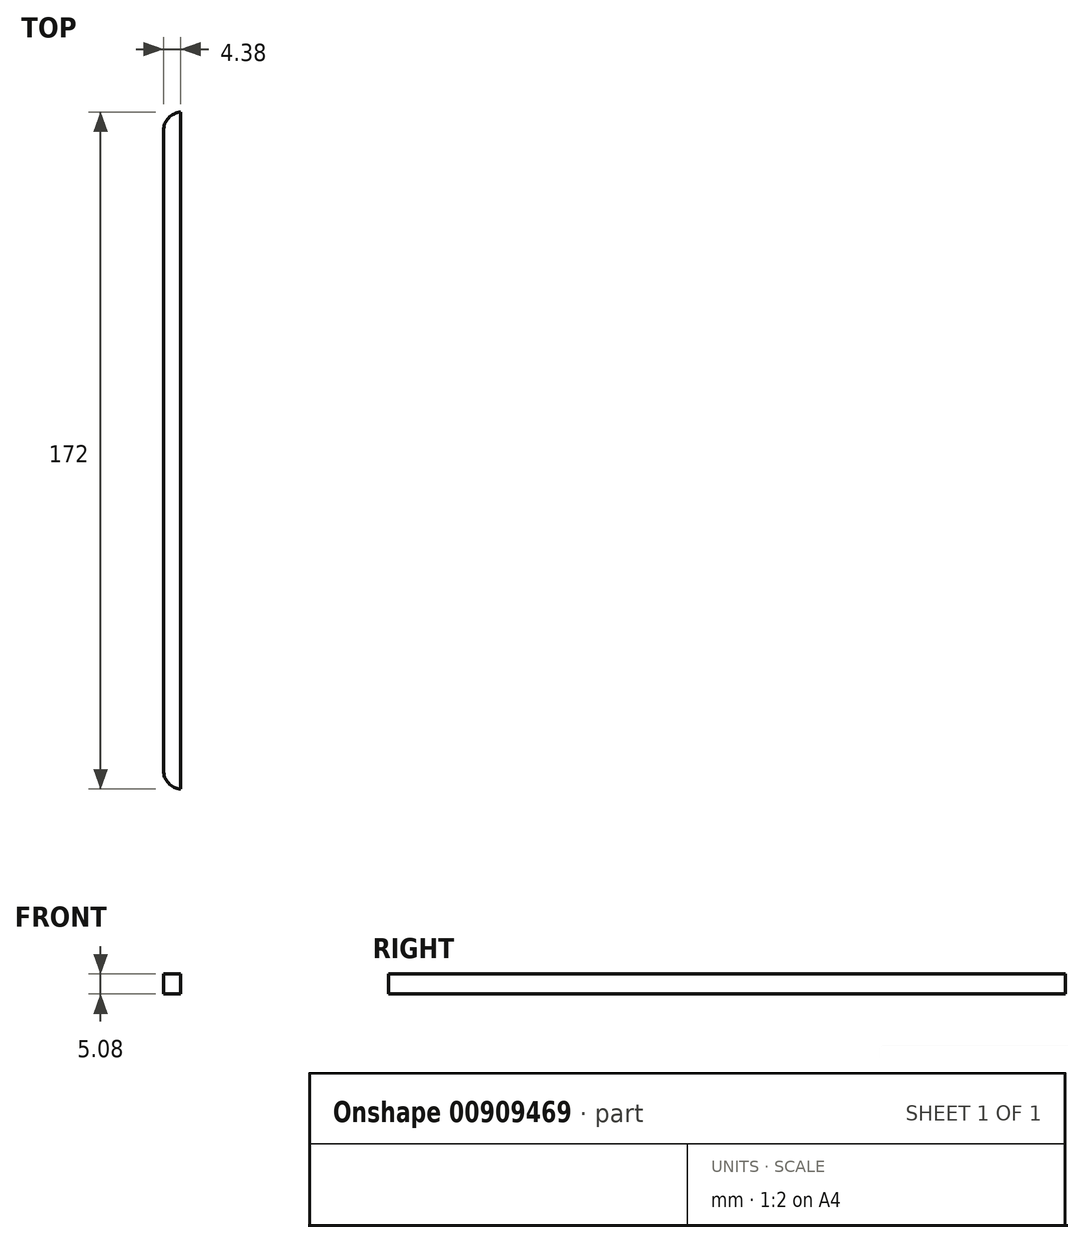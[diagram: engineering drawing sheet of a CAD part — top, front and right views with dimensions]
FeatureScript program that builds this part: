
annotation { "Feature Type Name" : "Feature", "Feature Type Description" : "" }
export const myFeature = defineFeature(function(context is Context, id is Id, definition is map)
    precondition{}
    {
        {
            var Q0;
            Q0=qCreatedBy(makeId("Top.planeOp"),FACE);
            var sketch = newSketch(context, id + "F0", { "sketchPlane" : qUnion([Q0])});
            skLineSegment(sketch, "E0.bottom", {"start": v(99.06, -99.06) * mm, "end": v(-99.06, -99.06) * mm});
            skLineSegment(sketch, "E0.top", {"start": v(99.06, 99.06) * mm, "end": v(-99.06, 99.06) * mm});
            skLineSegment(sketch, "E0.left", {"start": v(99.06, -99.06) * mm, "end": v(99.06, 99.06) * mm});
            skLineSegment(sketch, "E0.right", {"start": v(-99.06, -99.06) * mm, "end": v(-99.06, 99.06) * mm});
            skPoint(sketch, "E0.middle", {"position": v(0, 0) * mm});
            skLineSegment(sketch, "E1.bottom", {"start": v(86.36, 86.36) * mm, "end": v(-86.36, 86.36) * mm});
            skLineSegment(sketch, "E1.top", {"start": v(86.36, -86.36) * mm, "end": v(-86.36, -86.36) * mm});
            skLineSegment(sketch, "E1.left", {"start": v(86.36, 86.36) * mm, "end": v(86.36, -86.36) * mm});
            skLineSegment(sketch, "E1.right", {"start": v(-86.36, 86.36) * mm, "end": v(-86.36, -86.36) * mm});
            skSolve(sketch);
        }
        {
            var Q0;
            Q0=qCreatedBy(makeId("Top.planeOp"),FACE);
            cPlane(context, id + "F1", {"entities" : qUnion([Q0]), "cplaneType" : CPlaneType.OFFSET, "offset" : 6.35 * mm, "width" : 152.4 * mm, "height" : 152.4 * mm});
        }
        {
            var Q0;
            Q0=qCreatedBy(id+"F1.planeOp",FACE);
            var sketch = newSketch(context, id + "F2", { "sketchPlane" : qUnion([Q0])});
            skLineSegment(sketch, "E2.bottom", {"start": v(99.06, 99.06) * mm, "end": v(-99.06, 99.06) * mm});
            skLineSegment(sketch, "E2.top", {"start": v(99.06, -99.06) * mm, "end": v(-99.06, -99.06) * mm});
            skLineSegment(sketch, "E2.left", {"start": v(99.06, 99.06) * mm, "end": v(99.06, -99.06) * mm});
            skLineSegment(sketch, "E2.right", {"start": v(-99.06, 99.06) * mm, "end": v(-99.06, -99.06) * mm});
            skPoint(sketch, "E2.middle", {"position": v(0, 0) * mm});
            skLineSegment(sketch, "E3.bottom", {"start": v(92.71, 92.71) * mm, "end": v(-92.71, 92.71) * mm});
            skLineSegment(sketch, "E3.top", {"start": v(92.71, -92.71) * mm, "end": v(-92.71, -92.71) * mm});
            skLineSegment(sketch, "E3.left", {"start": v(92.71, 92.71) * mm, "end": v(92.71, -92.71) * mm});
            skLineSegment(sketch, "E3.right", {"start": v(-92.71, 92.71) * mm, "end": v(-92.71, -92.71) * mm});
            skSolve(sketch);
        }
        {
            var Q0;
            Q0=qCreatedBy(makeId("Front.planeOp"),FACE);
            var sketch = newSketch(context, id + "F3", { "sketchPlane" : qUnion([Q0])});
            skLineSegment(sketch, "E4.bottom", {"start": v(-137.33, -39.02) * mm, "end": v(163.38, -39.02) * mm});
            skLineSegment(sketch, "E4.top", {"start": v(-137.33, 123.29) * mm, "end": v(163.38, 123.29) * mm});
            skLineSegment(sketch, "E4.left", {"start": v(-137.33, -39.02) * mm, "end": v(-137.33, 123.29) * mm});
            skLineSegment(sketch, "E4.right", {"start": v(163.38, -39.02) * mm, "end": v(163.38, 123.29) * mm});
            skSolve(sketch);
        }
        {
            var Q0;
            Q0=qCreatedBy(makeId("Right.planeOp"),FACE);
            var sketch = newSketch(context, id + "F4", { "sketchPlane" : qUnion([Q0])});
            skLineSegment(sketch, "E5.bottom", {"start": v(-40.9, -45.65) * mm, "end": v(117.43, -45.65) * mm});
            skLineSegment(sketch, "E5.top", {"start": v(-40.9, 78.34) * mm, "end": v(117.43, 78.34) * mm});
            skLineSegment(sketch, "E5.left", {"start": v(-40.9, -45.65) * mm, "end": v(-40.9, 78.34) * mm});
            skLineSegment(sketch, "E5.right", {"start": v(117.43, -45.65) * mm, "end": v(117.43, 78.34) * mm});
            skSolve(sketch);
        }
        {
            var Q0;
            Q0=makeQuery(id+"FveU7qWkoDMfakH_0.opExtrude","CAP_FACE",FACE,{"disambiguationData":[OSD([sQuery(id+"F0.wireOp",EDGE,"E0.bottom"),sQuery(id+"F0.wireOp",EDGE,"E0.top"),sQuery(id+"F0.wireOp",EDGE,"E0.left"),sQuery(id+"F0.wireOp",EDGE,"E0.right"),sQuery(id+"F0.wireOp",EDGE,"E1.bottom"),sQuery(id+"F0.wireOp",EDGE,"E1.top"),sQuery(id+"F0.wireOp",EDGE,"E1.left"),sQuery(id+"F0.wireOp",EDGE,"E1.right")])],"isStart":false});
            var sketch = newSketch(context, id + "F5", { "sketchPlane" : qUnion([Q0])});
            skArc(sketch, "E6", {"start": v(-2.54, 90.8) * mm, "mid": v(-5.86, 89.53) * mm, "end": v(-2.54, 88.27) * mm});
            skLineSegment(sketch, "E7", {"start": v(-2.54, 90.8) * mm, "end": v(0, 90.8) * mm});
            skLineSegment(sketch, "E8", {"start": v(0, 90.8) * mm, "end": v(0, 88.27) * mm});
            skLineSegment(sketch, "E9", {"start": v(0, 88.27) * mm, "end": v(-2.54, 88.27) * mm});
            skLineSegment(sketch, "E10", {"start": v(0, 89.54) * mm, "end": v(-3.96, 89.54) * mm, "construction": true});
            skSolve(sketch);
        }
        {
            var Q0;
            Q0=makeQuery(id+"FveU7qWkoDMfakH_0.opExtrude","CAP_FACE",FACE,{"disambiguationData":[OSD([sQuery(id+"F0.wireOp",EDGE,"E0.bottom"),sQuery(id+"F0.wireOp",EDGE,"E0.top"),sQuery(id+"F0.wireOp",EDGE,"E0.left"),sQuery(id+"F0.wireOp",EDGE,"E0.right"),sQuery(id+"F0.wireOp",EDGE,"E1.bottom"),sQuery(id+"F0.wireOp",EDGE,"E1.top"),sQuery(id+"F0.wireOp",EDGE,"E1.left"),sQuery(id+"F0.wireOp",EDGE,"E1.right")])],"isStart":false});
            var sketch = newSketch(context, id + "F6", { "sketchPlane" : qUnion([Q0])});
            skArc(sketch, "E11", {"start": v(-90.8, -2.54) * mm, "mid": v(-89.53, -5.86) * mm, "end": v(-88.27, -2.54) * mm, "construction": true});
            skLineSegment(sketch, "E12", {"start": v(-88.27, -2.54) * mm, "end": v(-88.27, 0) * mm, "construction": true});
            skLineSegment(sketch, "E13", {"start": v(-88.27, 0) * mm, "end": v(-90.8, 0) * mm, "construction": true});
            skLineSegment(sketch, "E14", {"start": v(-90.8, 0) * mm, "end": v(-90.8, -2.54) * mm, "construction": true});
            skLineSegment(sketch, "E15", {"start": v(0, 90.8) * mm, "end": v(0, 88.27) * mm, "construction": true});
            skLineSegment(sketch, "E16", {"start": v(-89.53, 0) * mm, "end": v(-89.53, 7.06) * mm, "construction": true});
            skLineSegment(sketch, "E17.0", {"start": v(-88.5, -2.65) * mm, "end": v(-88.5, -0.23) * mm, "construction": true});
            skArc(sketch, "E17.1", {"start": v(-90.58, -2.65) * mm, "mid": v(-89.53, -5.64) * mm, "end": v(-88.5, -2.65) * mm, "construction": true});
            skLineSegment(sketch, "E17.2", {"start": v(-90.58, -0.23) * mm, "end": v(-90.58, -2.65) * mm, "construction": true});
            skLineSegment(sketch, "E17.3", {"start": v(-88.5, -0.23) * mm, "end": v(-90.58, -0.23) * mm, "construction": true});
            skLineSegment(sketch, "E18", {"start": v(-90.58, -2.65) * mm, "end": v(-90.58, 0) * mm});
            skLineSegment(sketch, "E19", {"start": v(-90.58, 0) * mm, "end": v(-88.5, 0) * mm});
            skLineSegment(sketch, "E20", {"start": v(-88.5, 0) * mm, "end": v(-88.5, -2.65) * mm});
            skArc(sketch, "E21", {"start": v(-90.58, -2.65) * mm, "mid": v(-89.53, -5.64) * mm, "end": v(-88.5, -2.65) * mm});
            skSolve(sketch);
        }
        {
            var Q0;
            Q0=makeQuery(id+"FspDqqNQahC62ZU_1.boolean.opBoolean","MERGE",FACE,{"derivedFrom":[makeQuery(id+"FveU7qWkoDMfakH_0.opExtrude","CAP_FACE",FACE,{"disambiguationData":[OSD([sQuery(id+"F0.wireOp",EDGE,"E0.bottom"),sQuery(id+"F0.wireOp",EDGE,"E0.top"),sQuery(id+"F0.wireOp",EDGE,"E0.left"),sQuery(id+"F0.wireOp",EDGE,"E0.right"),sQuery(id+"F0.wireOp",EDGE,"E1.bottom"),sQuery(id+"F0.wireOp",EDGE,"E1.top"),sQuery(id+"F0.wireOp",EDGE,"E1.left"),sQuery(id+"F0.wireOp",EDGE,"E1.right")])],"isStart":false}),makeQuery(id+"FspDqqNQahC62ZU_1.opExtrude","CAP_FACE",FACE,{"disambiguationData":[OSD([sQuery(id+"F6.wireOp",EDGE,"E18"),sQuery(id+"F6.wireOp",EDGE,"E19"),sQuery(id+"F6.wireOp",EDGE,"E20"),sQuery(id+"F6.wireOp",EDGE,"E21")])],"isStart":true})]});
            var sketch = newSketch(context, id + "F7", { "sketchPlane" : qUnion([Q0])});
            skLineSegment(sketch, "E22", {"start": v(0, 86.36) * mm, "end": v(-81.28, 86.36) * mm});
            skLineSegment(sketch, "E23", {"start": v(-86.36, 81.28) * mm, "end": v(-86.36, 0) * mm});
            skLineSegment(sketch, "E24", {"start": v(-85.25, -6.28) * mm, "end": v(-95.33, -6.28) * mm});
            skLineSegment(sketch, "E25", {"start": v(-95.33, -6.28) * mm, "end": v(-90.58, 0) * mm});
            skLineSegment(sketch, "E26", {"start": v(-90.58, 0) * mm, "end": v(-90.17, 0) * mm});
            skLineSegment(sketch, "E27", {"start": v(-90.17, 0) * mm, "end": v(-90.17, 81.28) * mm});
            skLineSegment(sketch, "E28", {"start": v(-86.36, 0) * mm, "end": v(-85.25, -6.28) * mm});
            skArc(sketch, "E29", {"start": v(-81.28, 90.17) * mm, "mid": v(-87.57, 87.57) * mm, "end": v(-90.17, 81.28) * mm});
            skArc(sketch, "E30", {"start": v(-81.28, 86.36) * mm, "mid": v(-84.87, 84.87) * mm, "end": v(-86.36, 81.28) * mm});
            skLineSegment(sketch, "E31", {"start": v(-81.28, 90.17) * mm, "end": v(-5.76, 90.17) * mm});
            skLineSegment(sketch, "E32", {"start": v(0, 86.36) * mm, "end": v(0, 88.27) * mm});
            skLineSegment(sketch, "E33", {"start": v(0, 88.27) * mm, "end": v(-2.54, 88.27) * mm});
            skArc(sketch, "E34", {"start": v(-5.76, 90.17) * mm, "mid": v(-4.93, 87.9) * mm, "end": v(-2.54, 88.27) * mm});
            skSolve(sketch);
        }
        {
            var Q0;
            {var subQ0=makeQuery(id+"FALStSsAS5Bzy6T_1.boolean.opBoolean","COPY",FACE,{"derivedFrom":makeQuery(id+"FALStSsAS5Bzy6T_1.opExtrude","CAP_FACE",FACE,{"disambiguationData":[OSD([sQuery(id+"F7.wireOp",EDGE,"E22"),sQuery(id+"F7.wireOp",EDGE,"E23"),sQuery(id+"F7.wireOp",EDGE,"E24"),sQuery(id+"F7.wireOp",EDGE,"E25"),sQuery(id+"F7.wireOp",EDGE,"E26"),sQuery(id+"F7.wireOp",EDGE,"E27"),sQuery(id+"F7.wireOp",EDGE,"E28"),sQuery(id+"F7.wireOp",EDGE,"E29"),sQuery(id+"F7.wireOp",EDGE,"E30"),sQuery(id+"F7.wireOp",EDGE,"E31"),sQuery(id+"F7.wireOp",EDGE,"E32"),sQuery(id+"F7.wireOp",EDGE,"E33"),sQuery(id+"F7.wireOp",EDGE,"E34")])],"isStart":false})});Q0=makeQuery(id+"FtahELFokxrj8ax_1.boolean.opBoolean","MERGE",FACE,{"derivedFrom":[subQ0,makeQuery(id+"FtahELFokxrj8ax_1.opPattern","COPY",FACE,{"derivedFrom":subQ0,"instanceName":"1"})]});}
            var sketch = newSketch(context, id + "F8", { "sketchPlane" : qUnion([Q0])});
            skLineSegment(sketch, "E35.bottom", {"start": v(-7.95, 90.17) * mm, "end": v(0, 90.17) * mm});
            skLineSegment(sketch, "E35.top", {"start": v(-7.95, 86.36) * mm, "end": v(0, 86.36) * mm});
            skLineSegment(sketch, "E35.left", {"start": v(-7.95, 90.17) * mm, "end": v(-7.95, 86.36) * mm});
            skLineSegment(sketch, "E35.right", {"start": v(0, 90.17) * mm, "end": v(0, 86.36) * mm});
            skSolve(sketch);
        }
        {
            var Q0;
            {var subQ0=makeQuery(id+"FspDqqNQahC62ZU_1.boolean.opBoolean","MERGE",FACE,{"derivedFrom":[makeQuery(id+"FveU7qWkoDMfakH_0.opExtrude","CAP_FACE",FACE,{"disambiguationData":[OSD([sQuery(id+"F0.wireOp",EDGE,"E0.bottom"),sQuery(id+"F0.wireOp",EDGE,"E0.top"),sQuery(id+"F0.wireOp",EDGE,"E0.left"),sQuery(id+"F0.wireOp",EDGE,"E0.right"),sQuery(id+"F0.wireOp",EDGE,"E1.bottom"),sQuery(id+"F0.wireOp",EDGE,"E1.top"),sQuery(id+"F0.wireOp",EDGE,"E1.left"),sQuery(id+"F0.wireOp",EDGE,"E1.right")])],"isStart":false}),makeQuery(id+"FspDqqNQahC62ZU_1.opExtrude","CAP_FACE",FACE,{"disambiguationData":[OSD([sQuery(id+"F6.wireOp",EDGE,"E18"),sQuery(id+"F6.wireOp",EDGE,"E19"),sQuery(id+"F6.wireOp",EDGE,"E20"),sQuery(id+"F6.wireOp",EDGE,"E21")])],"isStart":true})]});Q0=makeQuery(id+"FtahELFokxrj8ax_1.boolean.opBoolean","MERGE",FACE,{"derivedFrom":[subQ0,makeQuery(id+"FtahELFokxrj8ax_1.opPattern","COPY",FACE,{"derivedFrom":subQ0,"instanceName":"1"})]});}
            var sketch = newSketch(context, id + "F9", { "sketchPlane" : qUnion([Q0])});
            skLineSegment(sketch, "E36.bottom", {"start": v(-8.44, 90.17) * mm, "end": v(0, 90.17) * mm});
            skLineSegment(sketch, "E36.top", {"start": v(-8.44, 92.71) * mm, "end": v(0, 92.71) * mm});
            skLineSegment(sketch, "E36.left", {"start": v(-8.44, 90.17) * mm, "end": v(-8.44, 92.71) * mm});
            skLineSegment(sketch, "E36.right", {"start": v(0, 90.17) * mm, "end": v(0, 92.71) * mm});
            skSolve(sketch);
        }
        {
            var Q0;
            {var subQ0=makeQuery(id+"FALStSsAS5Bzy6T_1.boolean.opBoolean","COPY",FACE,{"derivedFrom":makeQuery(id+"FALStSsAS5Bzy6T_1.opExtrude","CAP_FACE",FACE,{"disambiguationData":[OSD([sQuery(id+"F7.wireOp",EDGE,"E22"),sQuery(id+"F7.wireOp",EDGE,"E23"),sQuery(id+"F7.wireOp",EDGE,"E24"),sQuery(id+"F7.wireOp",EDGE,"E25"),sQuery(id+"F7.wireOp",EDGE,"E26"),sQuery(id+"F7.wireOp",EDGE,"E27"),sQuery(id+"F7.wireOp",EDGE,"E28"),sQuery(id+"F7.wireOp",EDGE,"E29"),sQuery(id+"F7.wireOp",EDGE,"E30"),sQuery(id+"F7.wireOp",EDGE,"E31"),sQuery(id+"F7.wireOp",EDGE,"E32"),sQuery(id+"F7.wireOp",EDGE,"E33"),sQuery(id+"F7.wireOp",EDGE,"E34")])],"isStart":false})});Q0=makeQuery(id+"FmhqpuIFYOwMVqM_1.boolean.opBoolean","MERGE",FACE,{"derivedFrom":[makeQuery(id+"FtahELFokxrj8ax_1.boolean.opBoolean","MERGE",FACE,{"derivedFrom":[subQ0,makeQuery(id+"FtahELFokxrj8ax_1.opPattern","COPY",FACE,{"derivedFrom":subQ0,"instanceName":"1"})]}),makeQuery(id+"FmhqpuIFYOwMVqM_1.opExtrude","CAP_FACE",FACE,{"disambiguationData":[OSD([sQuery(id+"F8.wireOp",EDGE,"E35.bottom"),sQuery(id+"F8.wireOp",EDGE,"E35.top"),sQuery(id+"F8.wireOp",EDGE,"E35.left"),sQuery(id+"F8.wireOp",EDGE,"E35.right")])],"isStart":true})]});}
            var sketch = newSketch(context, id + "F10", { "sketchPlane" : qUnion([Q0])});
            skLineSegment(sketch, "E37", {"start": v(0, 88.5) * mm, "end": v(2.64, 88.5) * mm});
            skLineSegment(sketch, "E38", {"start": v(0, 90.63) * mm, "end": v(2.64, 90.63) * mm});
            skArc(sketch, "E39", {"start": v(2.64, 88.5) * mm, "mid": v(5.67, 89.56) * mm, "end": v(2.64, 90.63) * mm});
            skLineSegment(sketch, "E40", {"start": v(0, 88.5) * mm, "end": v(0, 90.63) * mm});
            skSolve(sketch);
        }
        {
            var Q0;
            Q0=makeQuery(id+"F9rfBv0o6nJ4J4G_1.boolean.opBoolean","MERGE",FACE,{"derivedFrom":[makeQuery(id+"FALStSsAS5Bzy6T_1.boolean.opBoolean","COPY",FACE,{"derivedFrom":makeQuery(id+"FALStSsAS5Bzy6T_1.opExtrude","SWEPT_FACE",FACE,{"disambiguationData":[OSD([sQuery(id+"F7.wireOp",EDGE,"E31")])]})}),makeQuery(id+"F9rfBv0o6nJ4J4G_1.opExtrude","SWEPT_FACE",FACE,{"disambiguationData":[OSD([sQuery(id+"F9.wireOp",EDGE,"E36.bottom")])]})]});
            var sketch = newSketch(context, id + "F11", { "sketchPlane" : qUnion([Q0])});
            skArc(sketch, "E41", {"start": v(-2.54, 73.98) * mm, "mid": v(-5.08, 76.52) * mm, "end": v(-7.62, 73.98) * mm});
            skArc(sketch, "E42", {"start": v(-7.62, 68.9) * mm, "mid": v(-5.08, 66.36) * mm, "end": v(-2.54, 68.9) * mm});
            skLineSegment(sketch, "E43", {"start": v(-7.62, 68.9) * mm, "end": v(-7.62, 73.98) * mm});
            skLineSegment(sketch, "E44", {"start": v(-2.54, 68.9) * mm, "end": v(-2.54, 73.98) * mm});
            skSolve(sketch);
        }
        {
            var Q0;
            Q0=qCreatedBy(makeId("Top.planeOp"),FACE);
            cPlane(context, id + "F12", {"entities" : qUnion([Q0]), "cplaneType" : CPlaneType.OFFSET, "offset" : 6.35 * mm, "width" : 152.4 * mm, "height" : 152.4 * mm});
        }
        {
            var Q0;
            Q0=qCreatedBy(id+"F12.planeOp",FACE);
            var sketch = newSketch(context, id + "F13", { "sketchPlane" : qUnion([Q0])});
            skLineSegment(sketch, "E45", {"start": v(-71.12, -86.36) * mm, "end": v(-81.28, -86.36) * mm});
            skLineSegment(sketch, "E46", {"start": v(-86.36, -81.28) * mm, "end": v(-86.36, -71.12) * mm});
            skArc(sketch, "E47", {"start": v(-86.36, -81.28) * mm, "mid": v(-84.87, -84.87) * mm, "end": v(-81.28, -86.36) * mm});
            skArc(sketch, "E48", {"start": v(-76.2, -81.28) * mm, "mid": v(-74.71, -84.87) * mm, "end": v(-71.12, -86.36) * mm});
            skPoint(sketch, "E48.startSnap0", {"position": v(-76.2, -86.36) * mm});
            skArc(sketch, "E49", {"start": v(-76.2, -81.28) * mm, "mid": v(-77.69, -77.69) * mm, "end": v(-81.28, -76.2) * mm});
            skArc(sketch, "E50", {"start": v(-86.36, -71.12) * mm, "mid": v(-84.87, -74.71) * mm, "end": v(-81.28, -76.2) * mm});
            skCircle(sketch, "E51", {"center": v(-81.28, -81.28) * mm, "radius": 2.54 * mm});
            skSolve(sketch);
        }
        {
            var Q0;
            Q0=makeQuery(id+"FMUYGmofN1sxITr_1.opExtrude","CAP_FACE",FACE,{"disambiguationData":[OSD([sQuery(id+"F13.wireOp",EDGE,"E45"),sQuery(id+"F13.wireOp",EDGE,"E46"),sQuery(id+"F13.wireOp",EDGE,"E47"),sQuery(id+"F13.wireOp",EDGE,"E48"),sQuery(id+"F13.wireOp",EDGE,"E49"),sQuery(id+"F13.wireOp",EDGE,"E50"),sQuery(id+"F13.wireOp",EDGE,"E51")])],"isStart":false});
            var sketch = newSketch(context, id + "F14", { "sketchPlane" : qUnion([Q0])});
            skCircle(sketch, "E52.cCircle", {"center": v(-81.28, -81.28) * mm, "radius": 4.11 * mm, "construction": true});
            skLineSegment(sketch, "E52.0", {"start": v(-84.64, -84.64) * mm, "end": v(-85.87, -80.05) * mm});
            skLineSegment(sketch, "E52.1", {"start": v(-85.87, -80.05) * mm, "end": v(-82.5, -76.7) * mm});
            skLineSegment(sketch, "E52.2", {"start": v(-82.5, -76.7) * mm, "end": v(-77.92, -77.92) * mm});
            skLineSegment(sketch, "E52.3", {"start": v(-77.92, -77.92) * mm, "end": v(-76.7, -82.5) * mm});
            skLineSegment(sketch, "E52.4", {"start": v(-76.7, -82.5) * mm, "end": v(-80.05, -85.87) * mm});
            skLineSegment(sketch, "E52.5", {"start": v(-80.05, -85.87) * mm, "end": v(-84.64, -84.64) * mm});
            skPoint(sketch, "E52.0.midPoint", {"position": v(-85.25, -82.34) * mm});
            skCircle(sketch, "E53.cCircle", {"center": v(-81.28, -81.28) * mm, "radius": 3.85 * mm, "construction": true});
            skLineSegment(sketch, "E53.0", {"start": v(-84.42, -84.42) * mm, "end": v(-85.57, -80.13) * mm, "construction": true});
            skLineSegment(sketch, "E53.1", {"start": v(-85.57, -80.13) * mm, "end": v(-82.43, -76.99) * mm, "construction": true});
            skLineSegment(sketch, "E53.2", {"start": v(-82.43, -76.99) * mm, "end": v(-78.14, -78.14) * mm, "construction": true});
            skLineSegment(sketch, "E53.3", {"start": v(-78.14, -78.14) * mm, "end": v(-76.99, -82.43) * mm, "construction": true});
            skLineSegment(sketch, "E53.4", {"start": v(-76.99, -82.43) * mm, "end": v(-80.13, -85.57) * mm, "construction": true});
            skLineSegment(sketch, "E53.5", {"start": v(-80.13, -85.57) * mm, "end": v(-84.42, -84.42) * mm, "construction": true});
            skPoint(sketch, "E53.0.midPoint", {"position": v(-85, -82.28) * mm});
            skLineSegment(sketch, "E54", {"start": v(-84.64, -84.64) * mm, "end": v(-84.87, -84.87) * mm});
            skSolve(sketch);
        }
        {
            var Q0;
            Q0=makeQuery(id+"FMUYGmofN1sxITr_1.opExtrude","CAP_FACE",FACE,{"disambiguationData":[OSD([sQuery(id+"F13.wireOp",EDGE,"E45"),sQuery(id+"F13.wireOp",EDGE,"E46"),sQuery(id+"F13.wireOp",EDGE,"E47"),sQuery(id+"F13.wireOp",EDGE,"E48"),sQuery(id+"F13.wireOp",EDGE,"E49"),sQuery(id+"F13.wireOp",EDGE,"E50"),sQuery(id+"F13.wireOp",EDGE,"E51")])],"isStart":false});
            var sketch = newSketch(context, id + "F15", { "sketchPlane" : qUnion([Q0])});
            skCircle(sketch, "E55.cCircle", {"center": v(-81.28, -81.28) * mm, "radius": 3.85 * mm, "construction": true});
            skLineSegment(sketch, "E55.0", {"start": v(-80.13, -85.57) * mm, "end": v(-84.42, -84.42) * mm});
            skLineSegment(sketch, "E55.1", {"start": v(-84.42, -84.42) * mm, "end": v(-85.57, -80.13) * mm});
            skLineSegment(sketch, "E55.2", {"start": v(-85.57, -80.13) * mm, "end": v(-82.43, -76.99) * mm});
            skLineSegment(sketch, "E55.3", {"start": v(-82.43, -76.99) * mm, "end": v(-78.14, -78.14) * mm});
            skLineSegment(sketch, "E55.4", {"start": v(-78.14, -78.14) * mm, "end": v(-76.99, -82.43) * mm});
            skLineSegment(sketch, "E55.5", {"start": v(-76.99, -82.43) * mm, "end": v(-80.13, -85.57) * mm});
            skPoint(sketch, "E55.0.midPoint", {"position": v(-82.28, -85) * mm});
            skCircle(sketch, "E56.cCircle", {"center": v(-81.28, -81.28) * mm, "radius": 4.11 * mm, "construction": true});
            skLineSegment(sketch, "E56.0", {"start": v(-85.87, -80.05) * mm, "end": v(-82.5, -76.7) * mm});
            skLineSegment(sketch, "E56.1", {"start": v(-82.5, -76.7) * mm, "end": v(-77.92, -77.92) * mm});
            skLineSegment(sketch, "E56.2", {"start": v(-77.92, -77.92) * mm, "end": v(-76.7, -82.5) * mm});
            skLineSegment(sketch, "E56.3", {"start": v(-76.7, -82.5) * mm, "end": v(-80.05, -85.87) * mm});
            skLineSegment(sketch, "E56.4", {"start": v(-80.05, -85.87) * mm, "end": v(-84.64, -84.64) * mm});
            skLineSegment(sketch, "E56.5", {"start": v(-84.64, -84.64) * mm, "end": v(-85.87, -80.05) * mm});
            skPoint(sketch, "E56.0.midPoint", {"position": v(-84.19, -78.37) * mm});
            skSolve(sketch);
        }
        {
            var Q0;
            Q0=makeQuery(id+"FCBoQjfW9jDOgKA_1.1.FjIP4lHeNLZtpzh_1.boolean.opBoolean","MERGE",FACE,{"derivedFrom":[makeQuery(id+"FCBoQjfW9jDOgKA_1.1.FMUYGmofN1sxITr_1.opExtrude","CAP_FACE",FACE,{"disambiguationData":[OSD([sQuery(id+"F13.wireOp",EDGE,"E45"),sQuery(id+"F13.wireOp",EDGE,"E46"),sQuery(id+"F13.wireOp",EDGE,"E47"),sQuery(id+"F13.wireOp",EDGE,"E48"),sQuery(id+"F13.wireOp",EDGE,"E49"),sQuery(id+"F13.wireOp",EDGE,"E50"),sQuery(id+"F13.wireOp",EDGE,"E51")])],"isStart":false}),makeQuery(id+"FCBoQjfW9jDOgKA_1.1.FjIP4lHeNLZtpzh_1.opExtrude","CAP_FACE",FACE,{"disambiguationData":[OSD([sQuery(id+"F15.wireOp",EDGE,"E55.0"),sQuery(id+"F15.wireOp",EDGE,"E55.1"),sQuery(id+"F15.wireOp",EDGE,"E55.2"),sQuery(id+"F15.wireOp",EDGE,"E55.3"),sQuery(id+"F15.wireOp",EDGE,"E55.4"),sQuery(id+"F15.wireOp",EDGE,"E55.5"),sQuery(id+"F15.wireOp",EDGE,"E56.0"),sQuery(id+"F15.wireOp",EDGE,"E56.1"),sQuery(id+"F15.wireOp",EDGE,"E56.2"),sQuery(id+"F15.wireOp",EDGE,"E56.3"),sQuery(id+"F15.wireOp",EDGE,"E56.4"),sQuery(id+"F15.wireOp",EDGE,"E56.5")])],"isStart":true})]});
            var sketch = newSketch(context, id + "F16", { "sketchPlane" : qUnion([Q0])});
            skLineSegment(sketch, "E57", {"start": v(-71.12, 86.36) * mm, "end": v(-81.28, 86.36) * mm});
            skLineSegment(sketch, "E58", {"start": v(-86.36, 71.12) * mm, "end": v(-86.36, 81.28) * mm});
            skArc(sketch, "E59", {"start": v(-81.28, 86.36) * mm, "mid": v(-84.87, 84.87) * mm, "end": v(-86.36, 81.28) * mm});
            skLineSegment(sketch, "E60", {"start": v(-86.36, -71.12) * mm, "end": v(-86.36, -81.28) * mm});
            skLineSegment(sketch, "E61", {"start": v(-71.12, -86.36) * mm, "end": v(-81.28, -86.36) * mm});
            skArc(sketch, "E62", {"start": v(-86.36, -81.28) * mm, "mid": v(-84.87, -84.87) * mm, "end": v(-81.28, -86.36) * mm});
            skArc(sketch, "E63", {"start": v(-71.12, -86.36) * mm, "mid": v(-73.48, -73.48) * mm, "end": v(-86.36, -71.12) * mm});
            skArc(sketch, "E64", {"start": v(-86.36, 71.12) * mm, "mid": v(-72.27, 72.27) * mm, "end": v(-71.12, 86.36) * mm});
            skSolve(sketch);
        }
        {
            var Q0;
            Q0=qCreatedBy(makeId("Top.planeOp"),FACE);
            var sketch = newSketch(context, id + "F17", { "sketchPlane" : qUnion([Q0])});
            skLineSegment(sketch, "E65", {"start": v(-86.36, 81.28) * mm, "end": v(-86.36, -81.28) * mm, "construction": true});
            skLineSegment(sketch, "E66", {"start": v(-81.28, -86.36) * mm, "end": v(-81.28, 86.36) * mm, "construction": true});
            skArc(sketch, "E67", {"start": v(-86.36, -81.28) * mm, "mid": v(-84.87, -84.87) * mm, "end": v(-81.28, -86.36) * mm, "construction": true});
            skArc(sketch, "E68", {"start": v(-81.28, 86.36) * mm, "mid": v(-84.87, 84.87) * mm, "end": v(-86.36, 81.28) * mm, "construction": true});
            skLineSegment(sketch, "E69.0", {"start": v(-86.01, 81.28) * mm, "end": v(-86.01, -81.28) * mm});
            skArc(sketch, "E69.1", {"start": v(-81.63, 86) * mm, "mid": v(-84.75, 84.5) * mm, "end": v(-86.01, 81.28) * mm});
            skLineSegment(sketch, "E69.2", {"start": v(-81.63, -86) * mm, "end": v(-81.63, 86) * mm});
            skArc(sketch, "E69.3", {"start": v(-86.01, -81.28) * mm, "mid": v(-84.75, -84.5) * mm, "end": v(-81.63, -86) * mm});
            skSolve(sketch);
        }
        {
            var Q0;
            Q0 = qSketchRegion(id + "F17", true);
            extrude(context, id + "F18", {"entities" : qUnion([Q0]), "depth" : 5.08 * mm, "offsetDistance" : 25.4 * mm});
        }
    });
